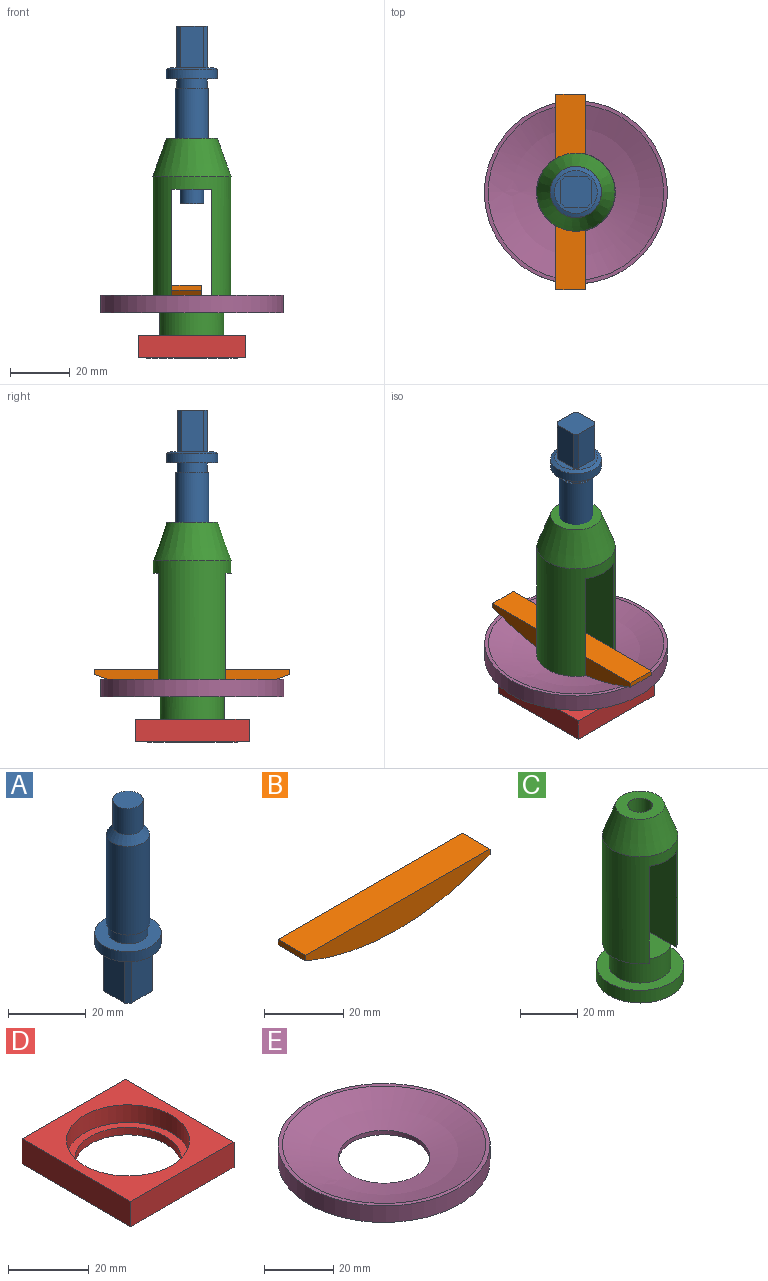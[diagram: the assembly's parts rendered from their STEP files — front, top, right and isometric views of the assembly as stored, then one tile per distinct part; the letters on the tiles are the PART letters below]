
ASSEMBLY  parts=5 mates=8
PART A: 19 faces, bbox 17.1x17.1x59.7 mm
  f0: plane 13.97x7.62mm, normal (0,1,0), area 106.5mm2, adj f4,f7,f10,f11
  f1: plane 13.97x7.62mm, normal (-1,0,0), area 106.5mm2, adj f4,f7,f11,f12
  f2: plane 13.97x7.62mm, normal (0,-1,0), area 106.5mm2, adj f4,f7,f12,f13
  f3: plane 13.97x7.62mm, normal (1,0,0), area 106.5mm2, adj f4,f7,f10,f13
  f4: plane 10.16x10.16mm, normal (0,0,-1), area 100mm2, adj f0,f1,f2,f3,f10,f11,f12,f13
  f5: cylinder r=8.57mm len=17.15mm, axis (0,0,-1), area 171mm2, adj f6,f9
  f6: cone r=8.57mm half-angle=65.4deg, axis (0,0,1), area 75.4mm2, adj f5,f7
  f7: plane 14.38x14.38mm, normal (0,0,-1), area 62.3mm2, adj f0,f1,f2,f3,f6,f10,f11,f12
  f8: cylinder r=5.08mm len=10.16mm, axis (0,0,-1), area 101.3mm2, adj f9,f14
  f9: plane 17.15x17.15mm, normal (0,0,1), area 149.8mm2, adj f5,f8
  f10: plane 13.97x1.27mm, normal (0.71,0.71,0), area 25.1mm2, adj f0,f3,f4,f7
  f11: plane 13.97x1.27mm, normal (-0.71,0.71,0), area 25.1mm2, adj f0,f1,f4,f7
  f12: plane 13.97x1.27mm, normal (-0.71,-0.71,0), area 25.1mm2, adj f1,f2,f4,f7
  f13: plane 13.97x1.27mm, normal (0.71,-0.71,0), area 25.1mm2, adj f2,f3,f4,f7
  f14: plane 11.18x11.18mm, normal (0,0,-1), area 17mm2, adj f8,f18
  f15: plane 7.87x7.87mm, normal (0,0,1), area 48.7mm2, adj f16
  f16: cylinder r=3.94mm len=8.26mm, axis (0,0,1), area 204.2mm2, adj f15,f17
  f17: cone r=5.59mm half-angle=33deg, axis (0,0,-1), area 90.7mm2, adj f16,f18
  f18: cylinder r=5.59mm len=27.94mm, axis (0,0,1), area 981mm2, adj f14,f17
PART B: 6 faces, bbox 65.5x9.9x8.4 mm
  f0: plane 9.91x1.71mm, normal (-1,0,0), area 17mm2, adj f1,f3,f4,f5
  f1: cylinder r=83.82mm len=65.53mm, axis (0,1,0), area 666.9mm2, adj f0,f2,f4,f5
  f2: plane 9.91x1.71mm, normal (1,0,0), area 17mm2, adj f1,f3,f4,f5
  f3: plane 65.53x9.91mm, normal (0,0,1), area 649.2mm2, adj f0,f2,f4,f5
  f4: plane 65.53x8.38mm, normal (0,-1,0), area 406mm2, adj f0,f1,f2,f3
  f5: plane 65.53x8.38mm, normal (0,1,0), area 406mm2, adj f0,f1,f2,f3
PART C: 16 faces, bbox 30.5x30.5x73.8 mm
  f0: cylinder r=13.14mm len=45.72mm, axis (0,0,-1), area 2605.7mm2, adj f1,f6,f8,f9,f10,f11
  f1: plane 22.58x6.41mm, normal (0,0,-1), area 54.7mm2, adj f0,f5,f11
  f2: cylinder r=15.24mm len=30.48mm, axis (0,0,-1), area 515.6mm2, adj f3,f4
  f3: plane 30.48x30.48mm, normal (0,0,1), area 363.6mm2, adj f2,f5
  f4: plane 30.48x30.48mm, normal (0,0,-1), area 698mm2, adj f2,f14
  f5: cylinder r=10.79mm len=21.59mm, axis (0,0,-1), area 668.4mm2, adj f1,f3,f6,f12
  f6: plane 22.58x6.41mm, normal (0,0,-1), area 54.7mm2, adj f0,f5,f10
  f7: plane 17.15x17.15mm, normal (0,0,1), area 172.6mm2, adj f8,f13
  f8: cone r=8.57mm half-angle=19.6deg, axis (0,0,-1), area 927.6mm2, adj f0,f7
  f9: plane 26.29x13.46mm, normal (0,0,-1), area 279.5mm2, adj f0,f10,f11,f13
  f10: plane 41.4x22.58mm, normal (1,0,0), area 934.9mm2, adj f0,f6,f9,f12
  f11: plane 41.4x22.58mm, normal (-1,0,0), area 934.9mm2, adj f0,f1,f9,f12
  f12: plane 21.59x13.46mm, normal (0,0,1), area 270.5mm2, adj f5,f10,f11
  f13: cylinder r=4.31mm len=17.12mm, axis (0,0,1), area 463.2mm2, adj f7,f9
  f14: cylinder r=3.17mm len=6.35mm, axis (0,0,-1), area 126.7mm2, adj f4,f15
  f15: plane 6.35x6.35mm, normal (0,0,-1), area 31.7mm2, adj f14
PART D: 9 faces, bbox 36.1x38.1x7.6 mm
  f0: cylinder r=13.14mm len=26.29mm, axis (0,0,-1), area 188.8mm2, adj f6,f8
  f1: plane 36.07x7.62mm, normal (0,1,0), area 274.8mm2, adj f2,f4,f5,f6
  f2: plane 38.1x7.62mm, normal (-1,0,0), area 290.3mm2, adj f1,f3,f5,f6
  f3: plane 36.07x7.62mm, normal (0,-1,0), area 274.8mm2, adj f2,f4,f5,f6
  f4: plane 38.1x7.62mm, normal (1,0,0), area 290.3mm2, adj f1,f3,f5,f6
  f5: plane 38.1x36.07mm, normal (0,0,1), area 644.5mm2, adj f1,f2,f3,f4,f7
  f6: plane 38.1x36.07mm, normal (0,0,-1), area 831.4mm2, adj f0,f1,f2,f3,f4
  f7: cylinder r=15.24mm len=30.48mm, axis (0,0,1), area 510.8mm2, adj f5,f8
  f8: plane 30.48x30.48mm, normal (0,0,1), area 186.9mm2, adj f0,f7
PART E: 5 faces, bbox 61.5x61.5x5.8 mm
  f0: cylinder r=13.27mm len=26.54mm, axis (0,0,-1), area 129.3mm2, adj f3,f4
  f1: cylinder r=30.73mm len=61.47mm, axis (0,0,-1), area 1128.1mm2, adj f2,f3
  f2: plane 61.47x61.47mm, normal (0,0,1), area 240.2mm2, adj f1,f4
  f3: plane 61.47x61.47mm, normal (0,0,-1), area 2414.1mm2, adj f0,f1
  f4: sphere r=83.82mm, area 2260.3mm2, adj f0,f2
PLACE A rot(axis=(1,0,0),180deg) t=(60.74,76.57,136.77)mm
PLACE B rot(axis=(0,0,1),90deg) t=(54.01,76.68,49.63)mm
PLACE C t=(60.74,76.57,25.22)mm
PLACE D rot(axis=(1,0,0),180deg) t=(60.74,76.57,32.89)mm
PLACE E t=(60.74,76.57,40.46)mm
MATE planar B.f5 <-> C.f10  axis (-1,0,0) through (54.01,76.68,46.21)mm
MATE planar D.f7 <-> C.f13  axis (0,0,-1) through (60.74,76.57,30.61)mm
MATE parallel B.f5 <-> C.f11  axis (-1,0,0) through (54.01,76.68,46.21)mm
MATE parallel B.f3 <-> C.f0  axis (0,0,1) through (58.96,109.45,49.63)mm
MATE cylindrical A.f5 <-> C.f13  axis (0,0,-1) through (60.74,76.57,87.88)mm
MATE cylindrical E.f0 <-> C.f0  axis (0,0,-1) through (60.74,76.57,41.24)mm
MATE planar C.f0 <-> E.f1  axis (0,0,-1) through (60.74,76.57,40.46)mm
MATE cylindrical D.f7 <-> C.f2  axis (0,0,-1) through (60.74,76.57,27.94)mm
